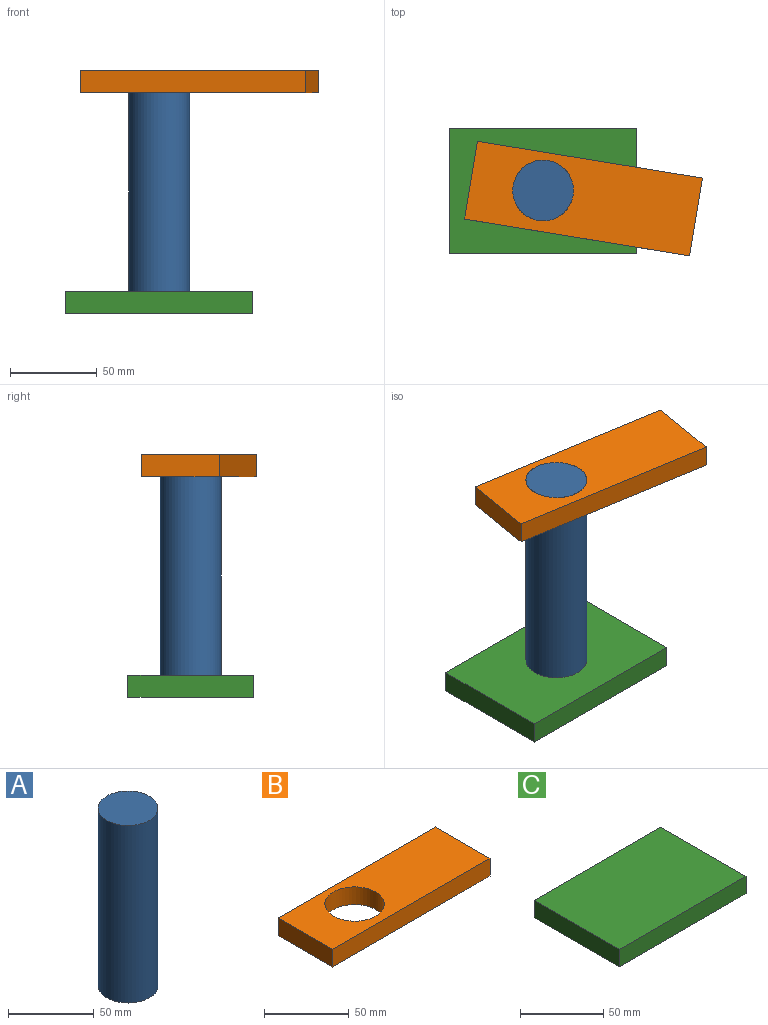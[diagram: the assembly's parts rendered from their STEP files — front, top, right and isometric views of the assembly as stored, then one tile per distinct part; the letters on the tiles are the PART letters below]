
ASSEMBLY  parts=3 mates=2
PART A: 3 faces, bbox 35x35x127 mm
  f0: cylinder r=17.51mm len=127mm, axis (0,0,-1), area 13969.1mm2, adj f1,f2
  f1: plane 35.01x35.01mm, normal (0,0,1), area 962.8mm2, adj f0
  f2: plane 35.01x35.01mm, normal (0,0,-1), area 962.8mm2, adj f0
PART B: 7 faces, bbox 131.3x45.4x12.7 mm
  f0: plane 45.35x12.7mm, normal (-1,0,0), area 576mm2, adj f1,f4,f5,f6
  f1: plane 131.26x12.7mm, normal (0,-1,0), area 1667mm2, adj f0,f2,f5,f6
  f2: plane 45.35x12.7mm, normal (1,0,0), area 576mm2, adj f1,f4,f5,f6
  f3: cylinder r=17.51mm len=35.01mm, axis (0,0,-1), area 1396.9mm2, adj f5,f6
  f4: plane 131.26x12.7mm, normal (0,1,0), area 1667mm2, adj f0,f2,f5,f6
  f5: plane 131.26x45.35mm, normal (0,0,1), area 4990.1mm2, adj f0,f1,f2,f3,f4
  f6: plane 131.26x45.35mm, normal (0,0,-1), area 4990.1mm2, adj f0,f1,f2,f3,f4
PART C: 6 faces, bbox 107.7x72.3x12.7 mm
  f0: plane 107.66x12.7mm, normal (0,1,0), area 1367.3mm2, adj f1,f3,f4,f5
  f1: plane 72.25x12.7mm, normal (-1,0,0), area 917.6mm2, adj f0,f2,f4,f5
  f2: plane 107.66x12.7mm, normal (0,-1,0), area 1367.3mm2, adj f1,f3,f4,f5
  f3: plane 72.25x12.7mm, normal (1,0,0), area 917.6mm2, adj f0,f2,f4,f5
  f4: plane 107.66x72.25mm, normal (0,0,1), area 7778.5mm2, adj f0,f1,f2,f3
  f5: plane 107.66x72.25mm, normal (0,0,-1), area 7778.5mm2, adj f0,f1,f2,f3
PLACE A t=(-25.15,20.35,25.6)mm
PLACE B rot(axis=(0,0,-1),9.3deg) t=(-25.15,20.35,12.9)mm
PLACE C t=(-25.15,20.35,12.9)mm fixed
MATE fastened C.f4 <-> A.f0  axis (0,0,1) through (-25.15,20.35,25.6)mm
MATE revolute B.f3 <-> A.f0  axis (0,0,-1) through (-25.15,20.35,152.6)mm
